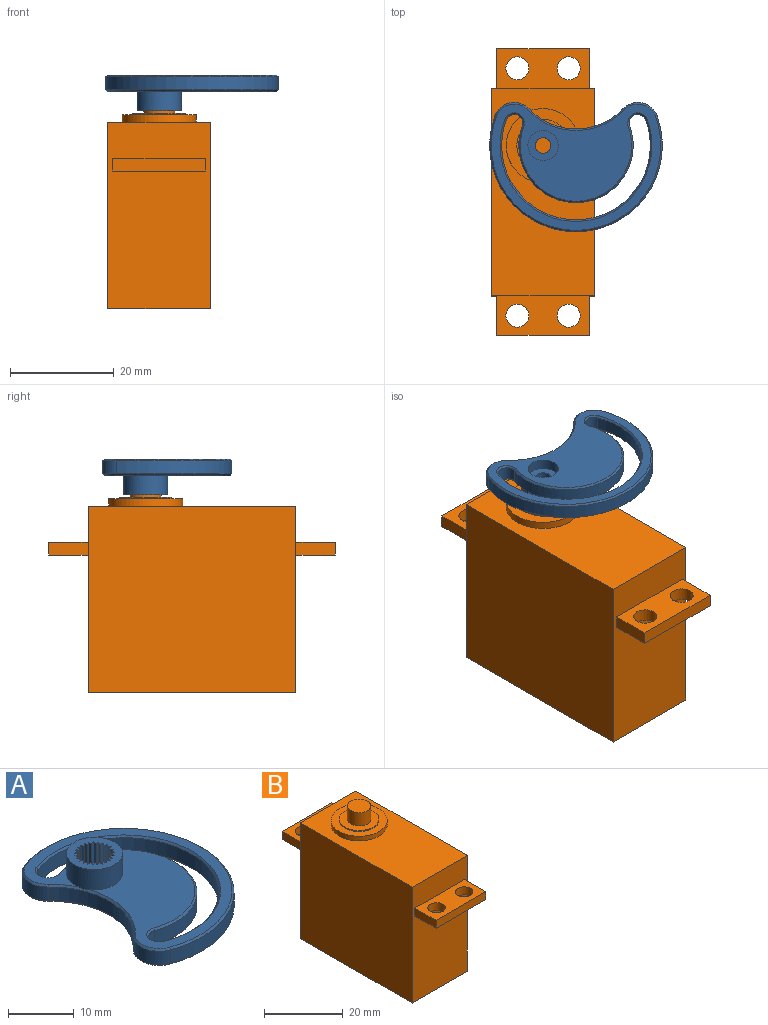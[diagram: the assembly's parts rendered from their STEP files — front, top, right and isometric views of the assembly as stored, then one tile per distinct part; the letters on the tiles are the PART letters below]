
ASSEMBLY  parts=2 mates=1
PART A: 82 faces, bbox 25x33.3x6.9 mm
  f0: cylinder r=1.5mm len=3mm, axis (0,0,-1), area 10.8mm2, adj f55,f65
  f1: plane 32.73x24.37mm, normal (0,0,1), area 336.5mm2, adj f53,f66,f67,f68,f69,f70,f71,f72
  f2: plane 32.73x24.37mm, normal (0,0,-1), area 366mm2, adj f64,f74,f75,f76,f77,f78,f79,f80
  f3: plane 3.75x0.52mm, normal (0.85,-0.52,0), area 2.3mm2, adj f4,f52,f54,f55
  f4: plane 3.75x0.52mm, normal (-0.85,-0.52,0), area 2.3mm2, adj f3,f5,f54,f55
  f5: plane 3.75x0.44mm, normal (0.7,-0.72,0), area 2.3mm2, adj f4,f6,f54,f55
  f6: plane 3.75x0.58mm, normal (-0.96,-0.3,0), area 2.3mm2, adj f5,f7,f54,f55
  f7: plane 3.75x0.53mm, normal (0.49,-0.87,0), area 2.3mm2, adj f6,f8,f54,f55
  f8: plane 3.75x0.61mm, normal (-1,-0.05,0), area 2.3mm2, adj f7,f9,f54,f55
  f9: plane 3.75x0.59mm, normal (0.26,-0.96,0), area 2.3mm2, adj f8,f10,f54,f55
  f10: plane 3.75x0.6mm, normal (-0.98,0.2,0), area 2.3mm2, adj f9,f11,f54,f55
  f11: plane 3.75x0.61mm, normal (0.01,-1,0), area 2.3mm2, adj f10,f12,f54,f55
  f12: plane 3.75x0.55mm, normal (-0.9,0.44,0), area 2.3mm2, adj f11,f13,f54,f55
  f13: plane 3.75x0.59mm, normal (-0.23,-0.97,0), area 2.3mm2, adj f12,f14,f54,f55
  f14: plane 3.75x0.46mm, normal (-0.76,0.65,0), area 2.3mm2, adj f13,f15,f54,f55
  f15: plane 3.75x0.54mm, normal (-0.47,-0.88,0), area 2.3mm2, adj f14,f16,f54,f55
  f16: plane 3.75x0.5mm, normal (-0.58,0.82,0), area 2.3mm2, adj f15,f17,f54,f55
  f17: plane 3.75x0.45mm, normal (-0.67,-0.74,0), area 2.3mm2, adj f16,f18,f54,f55
  f18: plane 3.75x0.57mm, normal (-0.35,0.94,0), area 2.3mm2, adj f17,f19,f54,f55
  f19: plane 3.75x0.51mm, normal (-0.84,-0.55,0), area 2.3mm2, adj f18,f20,f54,f55
  f20: plane 3.75x0.61mm, normal (-0.11,0.99,0), area 2.3mm2, adj f19,f21,f54,f55
  f21: plane 3.75x0.58mm, normal (-0.95,-0.32,0), area 2.3mm2, adj f20,f22,f54,f55
  f22: plane 3.75x0.6mm, normal (0.14,0.99,0), area 2.3mm2, adj f21,f23,f54,f55
  f23: plane 3.75x0.61mm, normal (-1,-0.08,0), area 2.3mm2, adj f22,f24,f54,f55
  f24: plane 3.75x0.56mm, normal (0.38,0.92,0), area 2.3mm2, adj f23,f25,f54,f55
  f25: plane 3.75x0.6mm, normal (-0.98,0.17,0), area 2.3mm2, adj f24,f26,f54,f55
  f26: plane 3.75x0.49mm, normal (0.6,0.8,0), area 2.3mm2, adj f25,f27,f54,f55
  f27: plane 3.75x0.56mm, normal (-0.91,0.41,0), area 2.3mm2, adj f26,f28,f54,f55
  f28: plane 3.75x0.48mm, normal (0.78,0.63,0), area 2.3mm2, adj f27,f29,f54,f55
  f29: plane 3.75x0.48mm, normal (-0.78,0.63,0), area 2.3mm2, adj f28,f30,f54,f55
  f30: plane 3.75x0.56mm, normal (0.91,0.41,0), area 2.3mm2, adj f29,f31,f54,f55
  f31: plane 3.75x0.49mm, normal (-0.6,0.8,0), area 2.3mm2, adj f30,f32,f54,f55
  f32: plane 3.75x0.6mm, normal (0.98,0.17,0), area 2.3mm2, adj f31,f33,f54,f55
  f33: plane 3.75x0.56mm, normal (-0.38,0.92,0), area 2.3mm2, adj f32,f34,f54,f55
  f34: plane 3.75x0.61mm, normal (1,-0.08,0), area 2.3mm2, adj f33,f35,f54,f55
  f35: plane 3.75x0.6mm, normal (-0.14,0.99,0), area 2.3mm2, adj f34,f36,f54,f55
  f36: plane 3.75x0.58mm, normal (0.95,-0.32,0), area 2.3mm2, adj f35,f37,f54,f55
  f37: plane 3.75x0.61mm, normal (0.11,0.99,0), area 2.3mm2, adj f36,f38,f54,f55
  f38: plane 3.75x0.51mm, normal (0.84,-0.55,0), area 2.3mm2, adj f37,f39,f54,f55
  f39: plane 3.75x0.57mm, normal (0.35,0.94,0), area 2.3mm2, adj f38,f40,f54,f55
  f40: plane 3.75x0.45mm, normal (0.67,-0.74,0), area 2.3mm2, adj f39,f41,f54,f55
  f41: plane 3.75x0.5mm, normal (0.58,0.82,0), area 2.3mm2, adj f40,f42,f54,f55
  f42: plane 3.75x0.54mm, normal (0.47,-0.88,0), area 2.3mm2, adj f41,f43,f54,f55
  f43: plane 3.75x0.46mm, normal (0.76,0.65,0), area 2.3mm2, adj f42,f44,f54,f55
  f44: plane 3.75x0.59mm, normal (0.23,-0.97,0), area 2.3mm2, adj f43,f45,f54,f55
  f45: plane 3.75x0.55mm, normal (0.9,0.44,0), area 2.3mm2, adj f44,f46,f54,f55
  f46: plane 3.75x0.61mm, normal (-0.01,-1,0), area 2.3mm2, adj f45,f47,f54,f55
  f47: plane 3.75x0.6mm, normal (0.98,0.2,0), area 2.3mm2, adj f46,f48,f54,f55
  f48: plane 3.75x0.59mm, normal (-0.26,-0.96,0), area 2.3mm2, adj f47,f49,f54,f55
  f49: plane 3.75x0.61mm, normal (1,-0.05,0), area 2.3mm2, adj f48,f50,f54,f55
  f50: plane 3.75x0.53mm, normal (-0.49,-0.87,0), area 2.3mm2, adj f49,f51,f54,f55
  f51: plane 3.75x0.58mm, normal (0.96,-0.3,0), area 2.3mm2, adj f50,f52,f54,f55
  f52: plane 3.75x0.44mm, normal (-0.7,-0.72,0), area 2.3mm2, adj f3,f51,f54,f55
  f53: cylinder r=4.25mm len=8.5mm, axis (0,0,-1), area 100.3mm2, adj f1,f54,f69
  f54: plane 8.5x8.5mm, normal (0,0,1), area 32.4mm2, adj f3,f4,f5,f6,f7,f8,f9,f10
  f55: plane 6.09x6.08mm, normal (0,0,1), area 17.3mm2, adj f0,f3,f4,f5,f6,f7,f8,f9
  f56: cylinder r=3.97mm len=6.6mm, axis (0,0,-1), area 20.7mm2, adj f57,f59,f68,f75
  f57: cylinder r=12.51mm len=18.12mm, axis (0,0,-1), area 52mm2, adj f56,f58,f69,f77
  f58: cylinder r=3.97mm len=6.6mm, axis (0,0,-1), area 20.7mm2, adj f57,f59,f67,f76
  f59: cylinder r=16.67mm len=33.34mm, axis (0,0,-1), area 164.2mm2, adj f56,f58,f66,f74
  f60: cylinder r=1.65mm len=3.2mm, axis (0,0,-1), area 13.3mm2, adj f61,f63,f71,f78
  f61: cylinder r=11.05mm len=22.1mm, axis (0,0,-1), area 108.8mm2, adj f60,f62,f73,f80
  f62: cylinder r=1.65mm len=3.2mm, axis (0,0,-1), area 13.3mm2, adj f61,f63,f72,f81
  f63: cylinder r=14.35mm len=28.7mm, axis (0,0,-1), area 141.4mm2, adj f60,f62,f70,f79
  f64: cylinder r=2.93mm len=5.87mm, axis (0,0,-1), area 37.5mm2, adj f2,f65
  f65: plane 5.87x5.87mm, normal (0,0,-1), area 20mm2, adj f0,f64
  f66: cone r=16.36mm half-angle=45deg, axis (0,0,-1), area 27.3mm2, adj f1,f59,f67,f68
  f67: cone r=3.66mm half-angle=45deg, axis (0,0,-1), area 3.3mm2, adj f1,f58,f66,f69
  f68: cone r=3.66mm half-angle=45deg, axis (0,0,-1), area 3.3mm2, adj f1,f56,f66,f69
  f69: cone r=12.51mm half-angle=45deg, axis (0,0,1), area 8.6mm2, adj f1,f53,f57,f67,f68
  f70: cone r=14.35mm half-angle=45deg, axis (0,0,1), area 24mm2, adj f1,f63,f71,f72
  f71: cone r=1.96mm half-angle=45deg, axis (0,0,1), area 2.4mm2, adj f1,f60,f70,f73
  f72: cone r=1.96mm half-angle=45deg, axis (0,0,1), area 2.4mm2, adj f1,f62,f70,f73
  f73: cone r=10.74mm half-angle=45deg, axis (0,0,-1), area 18mm2, adj f1,f61,f71,f72
  f74: cone r=16.36mm half-angle=45deg, axis (0,0,1), area 27.3mm2, adj f2,f59,f75,f76
  f75: cone r=3.66mm half-angle=45deg, axis (0,0,1), area 3.3mm2, adj f2,f56,f74,f77
  f76: cone r=3.66mm half-angle=45deg, axis (0,0,1), area 3.3mm2, adj f2,f58,f74,f77
  f77: cone r=12.51mm half-angle=45deg, axis (0,0,-1), area 8.8mm2, adj f2,f57,f75,f76
  f78: cone r=1.96mm half-angle=45deg, axis (0,0,-1), area 2.4mm2, adj f2,f60,f79,f80
  f79: cone r=14.35mm half-angle=45deg, axis (0,0,-1), area 24mm2, adj f2,f63,f78,f81
  f80: cone r=10.74mm half-angle=45deg, axis (0,0,1), area 18mm2, adj f2,f61,f78,f81
  f81: cone r=1.96mm half-angle=45deg, axis (0,0,-1), area 2.4mm2, adj f2,f62,f79,f80
PART B: 26 faces, bbox 19.9x55.4x42 mm
  f0: plane 36.07x19.86mm, normal (0,-1,0), area 672.3mm2, adj f1,f3,f4,f5,f19,f21,f24,f25
  f1: plane 40.13x36.07mm, normal (1,0,0), area 1447.5mm2, adj f0,f2,f4,f5
  f2: plane 36.07x19.86mm, normal (0,1,0), area 672.3mm2, adj f1,f3,f4,f5,f12,f16,f17,f18
  f3: plane 40.13x36.07mm, normal (-1,0,0), area 1447.5mm2, adj f0,f2,f4,f5
  f4: plane 40.13x19.86mm, normal (0,0,1), area 637.1mm2, adj f0,f1,f2,f3,f6
  f5: plane 40.13x19.86mm, normal (0,0,-1), area 797.1mm2, adj f0,f1,f2,f3
  f6: cylinder r=7.14mm len=14.28mm, axis (0,0,-1), area 64.9mm2, adj f4,f7
  f7: plane 14.28x14.27mm, normal (0,0,1), area 79.8mm2, adj f6,f8
  f8: cylinder r=5.05mm len=10.11mm, axis (0,0,-1), area 9.7mm2, adj f7,f9
  f9: plane 10.11x10.11mm, normal (0,0,1), area 52mm2, adj f8,f10
  f10: cylinder r=3mm len=6mm, axis (0,0,-1), area 78mm2, adj f9,f11
  f11: plane 6x6mm, normal (0,0,1), area 28.3mm2, adj f10
  f12: plane 7.62x2.46mm, normal (1,0,0), area 18.8mm2, adj f2,f13,f17,f18
  f13: plane 17.91x2.46mm, normal (0,1,0), area 44.1mm2, adj f12,f16,f17,f18
  f14: cylinder r=2.22mm len=4.45mm, axis (0,0,1), area 34.4mm2, adj f17,f18
  f15: cylinder r=2.22mm len=4.45mm, axis (0,0,1), area 34.4mm2, adj f17,f18
  f16: plane 7.62x2.46mm, normal (-1,0,0), area 18.8mm2, adj f2,f13,f17,f18
  f17: plane 17.91x7.62mm, normal (0,0,-1), area 105.4mm2, adj f2,f12,f13,f14,f15,f16
  f18: plane 17.91x7.62mm, normal (0,0,1), area 105.4mm2, adj f2,f12,f13,f14,f15,f16
  f19: plane 7.62x2.46mm, normal (-1,0,0), area 18.8mm2, adj f0,f20,f24,f25
  f20: plane 17.91x2.46mm, normal (0,-1,0), area 44.1mm2, adj f19,f21,f24,f25
  f21: plane 7.62x2.46mm, normal (1,0,0), area 18.8mm2, adj f0,f20,f24,f25
  f22: cylinder r=2.22mm len=4.45mm, axis (0,0,1), area 34.4mm2, adj f24,f25
  f23: cylinder r=2.22mm len=4.45mm, axis (0,0,1), area 34.4mm2, adj f24,f25
  f24: plane 17.91x7.62mm, normal (0,0,-1), area 105.4mm2, adj f0,f19,f20,f21,f22,f23
  f25: plane 17.91x7.62mm, normal (0,0,1), area 105.4mm2, adj f0,f19,f20,f21,f22,f23
PLACE A rot(axis=(-0.71,0.71,0),180deg) t=(4.95,-14.92,12.88)mm
PLACE B t=(4.95,-23.88,-29.08)mm
MATE revolute A.f0 <-> B.f10  axis (0,0,-1) through (4.95,-14.92,12.88)mm
